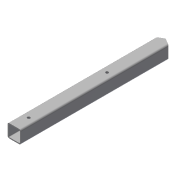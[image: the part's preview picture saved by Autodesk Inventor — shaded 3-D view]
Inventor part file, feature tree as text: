
AUTODESK INVENTOR PART (.ipt)
format: ipt  version: 2016 (Build 200138000, 138)  size: 129,024 bytes
history: native  units: in
note: dims shown in document units (in); Inventor stores cm internally (conversion verified against a paired STEP export)
features: sketch x4, extrude x2, hole x2
ambient origin geometry x8: Origin, YZ Plane, XZ Plane, XY Plane, X Axis, Y Axis, Z Axis, Center Point
bodies: Solid1 (feature_tree)
feature tree (8):
  extrude  "tube"  Depth=1.0in
  hole  "centerHole_cutOff"  [1 undecoded]
  hole  "armHoles"  [1 undecoded]
  extrude  "Extrusion4"  Depth=0.3937in
  sketch  "Sketch1"  dims[d0=1.0in d2=1.0in]
  sketch  "Sketch7"  dims[d3=0.125in d4=0.0787in]
  sketch  "Sketch8"  dims[d5=12.9961in d6=0.0in d45=1.0in]
  sketch  "Sketch9"  dims[d46=0.25in d47=0.75in d48=0.375in d49=0.25in d50=0.5635in d51=1.0in d52=0.8108in d53=0.7874in d55=5.9055in d56=0.3937in d58=1.0in d60=5.0in d61=0.2165in d62=0.75in d63=0.375in d64=0.25in d65=0.5635in d66=1.0in d67=0.8108in d68=0.578in d70=30.0deg d71=2.0in d72=0.0in]
note: 2 required parameter values undecoded (feature->parameter linkage not recoverable at this tier; creation-order binding heuristic only, values carry confidence <= 0.55)
